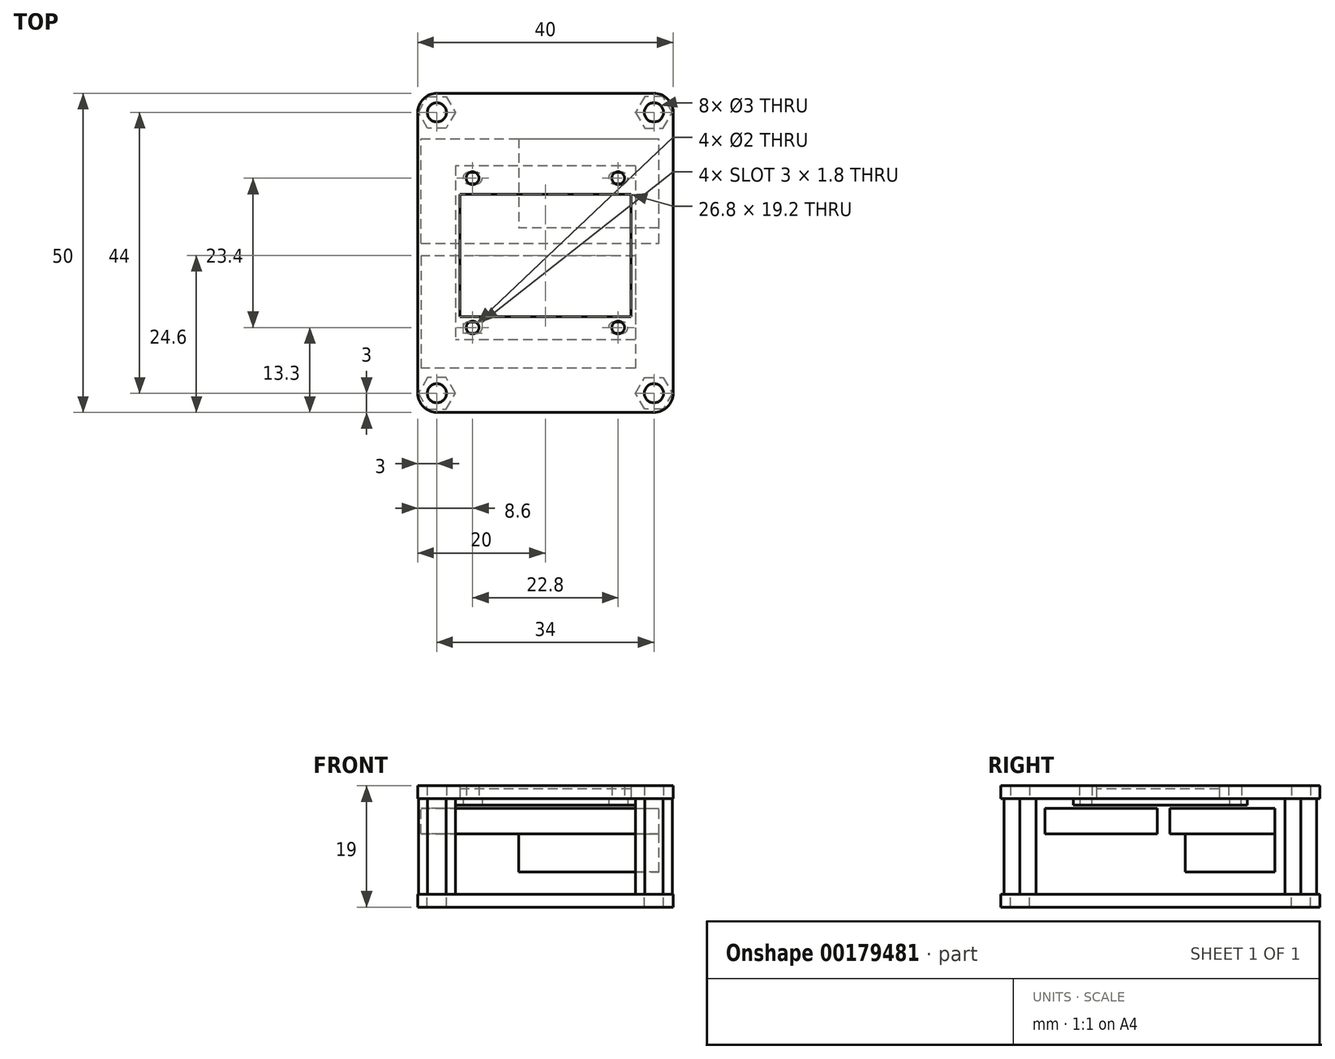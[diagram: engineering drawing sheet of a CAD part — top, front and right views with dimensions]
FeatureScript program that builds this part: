
annotation { "Feature Type Name" : "Feature", "Feature Type Description" : "" }
export const myFeature = defineFeature(function(context is Context, id is Id, definition is map)
    precondition{}
    {
        {
            var Q0;
            Q0=qCreatedBy(makeId("Top.planeOp"),FACE);
            var sketch = newSketch(context, id + "F0", { "sketchPlane" : qUnion([Q0])});
            skLineSegment(sketch, "E0.bottom", {"start": v(14.1, 13.6) * mm, "end": v(-14.1, 13.6) * mm});
            skLineSegment(sketch, "E0.top", {"start": v(14.1, -13.6) * mm, "end": v(-14.1, -13.6) * mm});
            skLineSegment(sketch, "E0.left", {"start": v(14.1, 13.6) * mm, "end": v(14.1, -13.6) * mm});
            skLineSegment(sketch, "E0.right", {"start": v(-14.1, 13.6) * mm, "end": v(-14.1, -13.6) * mm});
            skPoint(sketch, "E0.middle", {"position": v(0, 0) * mm});
            skArc(sketch, "E1", {"start": v(-12, 12.6) * mm, "mid": v(-12.9, 11.7) * mm, "end": v(-12, 10.8) * mm});
            skArc(sketch, "E2", {"start": v(-10.8, 10.8) * mm, "mid": v(-9.9, 11.7) * mm, "end": v(-10.8, 12.6) * mm});
            skPoint(sketch, "E3", {"position": v(-12.9, 11.7) * mm});
            skPoint(sketch, "E4", {"position": v(-9.9, 11.7) * mm});
            skLineSegment(sketch, "E5", {"start": v(-12, 12.6) * mm, "end": v(-10.8, 12.6) * mm});
            skLineSegment(sketch, "E6", {"start": v(-12, 10.8) * mm, "end": v(-10.8, 10.8) * mm});
            skLineSegment(sketch, "E7", {"start": v(0, 0) * mm, "end": v(0, 3.9) * mm, "construction": true});
            skPoint(sketch, "E8.MirrorP", {"position": v(12.9, 11.7) * mm});
            skPoint(sketch, "E9.MirrorP", {"position": v(9.9, 11.7) * mm});
            skLineSegment(sketch, "E10.MirrorCS", {"start": v(12, 10.8) * mm, "end": v(10.8, 10.8) * mm});
            skArc(sketch, "E11.MirrorCS", {"start": v(12, 12.6) * mm, "mid": v(12.9, 11.7) * mm, "end": v(12, 10.8) * mm});
            skArc(sketch, "E12.MirrorCS", {"start": v(10.8, 10.8) * mm, "mid": v(9.9, 11.7) * mm, "end": v(10.8, 12.6) * mm});
            skLineSegment(sketch, "E13.MirrorCS", {"start": v(12, 12.6) * mm, "end": v(10.8, 12.6) * mm});
            skLineSegment(sketch, "E14", {"start": v(0, 0) * mm, "end": v(-3.91, 0) * mm, "construction": true});
            skLineSegment(sketch, "E15.MirrorCS", {"start": v(-12, -12.6) * mm, "end": v(-10.8, -12.6) * mm});
            skLineSegment(sketch, "E16.MirrorCS", {"start": v(-12, -10.8) * mm, "end": v(-10.8, -10.8) * mm});
            skLineSegment(sketch, "E17.MirrorCS", {"start": v(12, -10.8) * mm, "end": v(10.8, -10.8) * mm});
            skLineSegment(sketch, "E18.MirrorCS", {"start": v(12, -12.6) * mm, "end": v(10.8, -12.6) * mm});
            skArc(sketch, "E19.MirrorCS", {"start": v(-12, -12.6) * mm, "mid": v(-12.9, -11.7) * mm, "end": v(-12, -10.8) * mm});
            skArc(sketch, "E20.MirrorCS", {"start": v(-10.8, -10.8) * mm, "mid": v(-9.9, -11.7) * mm, "end": v(-10.8, -12.6) * mm});
            skArc(sketch, "E21.MirrorCS", {"start": v(12, -12.6) * mm, "mid": v(12.9, -11.7) * mm, "end": v(12, -10.8) * mm});
            skArc(sketch, "E22.MirrorCS", {"start": v(10.8, -10.8) * mm, "mid": v(9.9, -11.7) * mm, "end": v(10.8, -12.6) * mm});
            skPoint(sketch, "E23.MirrorP", {"position": v(12.9, -11.7) * mm});
            skPoint(sketch, "E24.MirrorP", {"position": v(-9.9, -11.7) * mm});
            skPoint(sketch, "E25.MirrorP", {"position": v(9.9, -11.7) * mm});
            skPoint(sketch, "E26.MirrorP", {"position": v(-12.9, -11.7) * mm});
            skSolve(sketch);
        }
        {
            var Q0;
            Q0 = qSketchRegion(id + "F0", true);
            extrude(context, id + "F1", {"entities" : qUnion([Q0]), "depth" : 1 * mm});
        }
        {
            var Q0;
            Q0=makeQuery(id+"F1.opExtrude","CAP_FACE",FACE,{"disambiguationData":[OSD([sQuery(id+"F0.wireOp",EDGE,"E0.bottom"),sQuery(id+"F0.wireOp",EDGE,"E0.top"),sQuery(id+"F0.wireOp",EDGE,"E0.left"),sQuery(id+"F0.wireOp",EDGE,"E0.right"),sQuery(id+"F0.wireOp",EDGE,"E1"),sQuery(id+"F0.wireOp",EDGE,"E2"),sQuery(id+"F0.wireOp",EDGE,"E5"),sQuery(id+"F0.wireOp",EDGE,"E6"),sQuery(id+"F0.wireOp",EDGE,"E10.MirrorCS"),sQuery(id+"F0.wireOp",EDGE,"E11.MirrorCS"),sQuery(id+"F0.wireOp",EDGE,"E12.MirrorCS"),sQuery(id+"F0.wireOp",EDGE,"E13.MirrorCS"),sQuery(id+"F0.wireOp",EDGE,"E15.MirrorCS"),sQuery(id+"F0.wireOp",EDGE,"E16.MirrorCS"),sQuery(id+"F0.wireOp",EDGE,"E17.MirrorCS"),sQuery(id+"F0.wireOp",EDGE,"E18.MirrorCS"),sQuery(id+"F0.wireOp",EDGE,"E19.MirrorCS"),sQuery(id+"F0.wireOp",EDGE,"E20.MirrorCS"),sQuery(id+"F0.wireOp",EDGE,"E21.MirrorCS"),sQuery(id+"F0.wireOp",EDGE,"E22.MirrorCS")])],"isStart":false});
            var sketch = newSketch(context, id + "F2", { "sketchPlane" : qUnion([Q0])});
            skLineSegment(sketch, "E27.bottom", {"start": v(13.4, 9.2) * mm, "end": v(-13.4, 9.2) * mm});
            skLineSegment(sketch, "E27.top", {"start": v(13.4, -10) * mm, "end": v(-13.4, -10) * mm});
            skLineSegment(sketch, "E27.left", {"start": v(13.4, 9.2) * mm, "end": v(13.4, -10) * mm});
            skLineSegment(sketch, "E27.right", {"start": v(-13.4, 9.2) * mm, "end": v(-13.4, -10) * mm});
            skPoint(sketch, "E27.middle", {"position": v(0, -0.4) * mm});
            skSolve(sketch);
        }
        {
            var Q0;
            Q0 = qSketchRegion(id + "F2", true);
            extrude(context, id + "F3", {"entities" : qUnion([Q0]), "operationType" : NewBodyOperationType.ADD, "depth" : 1.5 * mm});
        }
        {
            var Q0;
            Q0=makeQuery(id+"F1.opExtrude","CAP_FACE",FACE,{"disambiguationData":[OSD([sQuery(id+"F0.wireOp",EDGE,"E0.bottom"),sQuery(id+"F0.wireOp",EDGE,"E0.top"),sQuery(id+"F0.wireOp",EDGE,"E0.left"),sQuery(id+"F0.wireOp",EDGE,"E0.right"),sQuery(id+"F0.wireOp",EDGE,"E1"),sQuery(id+"F0.wireOp",EDGE,"E2"),sQuery(id+"F0.wireOp",EDGE,"E5"),sQuery(id+"F0.wireOp",EDGE,"E6"),sQuery(id+"F0.wireOp",EDGE,"E10.MirrorCS"),sQuery(id+"F0.wireOp",EDGE,"E11.MirrorCS"),sQuery(id+"F0.wireOp",EDGE,"E12.MirrorCS"),sQuery(id+"F0.wireOp",EDGE,"E13.MirrorCS"),sQuery(id+"F0.wireOp",EDGE,"E15.MirrorCS"),sQuery(id+"F0.wireOp",EDGE,"E16.MirrorCS"),sQuery(id+"F0.wireOp",EDGE,"E17.MirrorCS"),sQuery(id+"F0.wireOp",EDGE,"E18.MirrorCS"),sQuery(id+"F0.wireOp",EDGE,"E19.MirrorCS"),sQuery(id+"F0.wireOp",EDGE,"E20.MirrorCS"),sQuery(id+"F0.wireOp",EDGE,"E21.MirrorCS"),sQuery(id+"F0.wireOp",EDGE,"E22.MirrorCS")])],"isStart":false});
            var sketch = newSketch(context, id + "F4", { "sketchPlane" : qUnion([Q0])});
            skLineSegment(sketch, "E28.bottom", {"start": v(17, 25) * mm, "end": v(-17, 25) * mm});
            skLineSegment(sketch, "E28.top", {"start": v(17, -25) * mm, "end": v(-17, -25) * mm});
            skLineSegment(sketch, "E28.left", {"start": v(20, 22) * mm, "end": v(20, -22) * mm});
            skLineSegment(sketch, "E28.right", {"start": v(-20, 22) * mm, "end": v(-20, -22) * mm});
            skPoint(sketch, "E28.middle", {"position": v(0, 0) * mm});
            skLineSegment(sketch, "E29", {"start": v(-12.9, 11.7) * mm, "end": v(-9.9, 11.7) * mm, "construction": true});
            skCircle(sketch, "E30", {"center": v(-11.4, 11.7) * mm, "radius": 1 * mm});
            skLineSegment(sketch, "E31", {"start": v(0, 0) * mm, "end": v(0, 2.9) * mm, "construction": true});
            skLineSegment(sketch, "E32", {"start": v(0, 0) * mm, "end": v(-3.26, 0) * mm, "construction": true});
            skCircle(sketch, "E33.MirrorC", {"center": v(11.4, 11.7) * mm, "radius": 1 * mm});
            skCircle(sketch, "E34.MirrorC", {"center": v(-11.4, -11.7) * mm, "radius": 1 * mm});
            skCircle(sketch, "E35.MirrorC", {"center": v(11.4, -11.7) * mm, "radius": 1 * mm});
            skCircle(sketch, "E36", {"center": v(-17, 22) * mm, "radius": 1.5 * mm});
            skPoint(sketch, "E37.visualSharp", {"position": v(-20, 25) * mm});
            skArc(sketch, "E37.filletArc", {"start": v(-17, 25) * mm, "mid": v(-19.12, 24.12) * mm, "end": v(-20, 22) * mm});
            skPoint(sketch, "E38.visualSharp", {"position": v(20, 25) * mm});
            skArc(sketch, "E38.filletArc", {"start": v(20, 22) * mm, "mid": v(19.12, 24.12) * mm, "end": v(17, 25) * mm});
            skPoint(sketch, "E39.visualSharp", {"position": v(20, -25) * mm});
            skArc(sketch, "E39.filletArc", {"start": v(17, -25) * mm, "mid": v(19.12, -24.12) * mm, "end": v(20, -22) * mm});
            skPoint(sketch, "E40.visualSharp", {"position": v(-20, -25) * mm});
            skArc(sketch, "E40.filletArc", {"start": v(-20, -22) * mm, "mid": v(-19.12, -24.12) * mm, "end": v(-17, -25) * mm});
            skCircle(sketch, "E41", {"center": v(17, 22) * mm, "radius": 1.5 * mm});
            skCircle(sketch, "E42", {"center": v(-17, -22) * mm, "radius": 1.5 * mm});
            skCircle(sketch, "E43", {"center": v(17, -22) * mm, "radius": 1.5 * mm});
            skLineSegment(sketch, "E44.bottom", {"start": v(-13.4, 9.2) * mm, "end": v(13.4, 9.2) * mm});
            skLineSegment(sketch, "E44.top", {"start": v(-13.4, -10) * mm, "end": v(13.4, -10) * mm});
            skLineSegment(sketch, "E44.left", {"start": v(-13.4, 9.2) * mm, "end": v(-13.4, -10) * mm});
            skLineSegment(sketch, "E44.right", {"start": v(13.4, 9.2) * mm, "end": v(13.4, -10) * mm});
            skSolve(sketch);
        }
        {
            var Q0;
            Q0 = qSketchRegion(id + "F4", true);
            extrude(context, id + "F5", {"entities" : qUnion([Q0]), "depth" : 2 * mm});
        }
        {
            var Q0;
            Q0=makeQuery(id+"F1.opExtrude","CAP_FACE",FACE,{"disambiguationData":[OSD([sQuery(id+"F0.wireOp",EDGE,"E0.bottom"),sQuery(id+"F0.wireOp",EDGE,"E0.top"),sQuery(id+"F0.wireOp",EDGE,"E0.left"),sQuery(id+"F0.wireOp",EDGE,"E0.right"),sQuery(id+"F0.wireOp",EDGE,"E1"),sQuery(id+"F0.wireOp",EDGE,"E2"),sQuery(id+"F0.wireOp",EDGE,"E5"),sQuery(id+"F0.wireOp",EDGE,"E6"),sQuery(id+"F0.wireOp",EDGE,"E10.MirrorCS"),sQuery(id+"F0.wireOp",EDGE,"E11.MirrorCS"),sQuery(id+"F0.wireOp",EDGE,"E12.MirrorCS"),sQuery(id+"F0.wireOp",EDGE,"E13.MirrorCS"),sQuery(id+"F0.wireOp",EDGE,"E15.MirrorCS"),sQuery(id+"F0.wireOp",EDGE,"E16.MirrorCS"),sQuery(id+"F0.wireOp",EDGE,"E17.MirrorCS"),sQuery(id+"F0.wireOp",EDGE,"E18.MirrorCS"),sQuery(id+"F0.wireOp",EDGE,"E19.MirrorCS"),sQuery(id+"F0.wireOp",EDGE,"E20.MirrorCS"),sQuery(id+"F0.wireOp",EDGE,"E21.MirrorCS"),sQuery(id+"F0.wireOp",EDGE,"E22.MirrorCS")])],"isStart":true});
            cPlane(context, id + "F6", {"entities" : qUnion([Q0]), "cplaneType" : CPlaneType.OFFSET, "offset" : 0.5 * mm, "width" : 150 * mm, "height" : 150 * mm});
        }
        {
            var Q0;
            Q0=qCreatedBy(id+"F6.planeOp",FACE);
            var sketch = newSketch(context, id + "F7", { "sketchPlane" : qUnion([Q0])});
            skLineSegment(sketch, "E45.bottom", {"start": v(14.1, 0.5) * mm, "end": v(-19.5, 0.5) * mm});
            skLineSegment(sketch, "E45.top", {"start": v(14.1, 18.1) * mm, "end": v(-19.5, 18.1) * mm});
            skLineSegment(sketch, "E45.left", {"start": v(14.1, 0.5) * mm, "end": v(14.1, 18.1) * mm});
            skLineSegment(sketch, "E45.right", {"start": v(-19.5, 0.5) * mm, "end": v(-19.5, 18.1) * mm});
            skLineSegment(sketch, "E46.0", {"start": v(14.1, -13.6) * mm, "end": v(14.1, 13.6) * mm, "construction": true});
            skLineSegment(sketch, "E47.bottom", {"start": v(-19.5, -1.5) * mm, "end": v(17.8, -1.5) * mm});
            skLineSegment(sketch, "E47.top", {"start": v(-19.5, -17.9) * mm, "end": v(17.8, -17.9) * mm});
            skLineSegment(sketch, "E47.left", {"start": v(-19.5, -1.5) * mm, "end": v(-19.5, -17.9) * mm});
            skLineSegment(sketch, "E47.right", {"start": v(17.8, -1.5) * mm, "end": v(17.8, -17.9) * mm});
            skSolve(sketch);
        }
        {
            var Q0;
            Q0 = qSketchRegion(id + "F7", true);
            extrude(context, id + "F8", {"entities" : qUnion([Q0]), "depth" : 4 * mm});
        }
        {
            var Q0;
            Q0=makeQuery(id+"F8.opExtrude","CAP_FACE",FACE,{"disambiguationData":[OSD([sQuery(id+"F7.wireOp",EDGE,"E47.bottom"),sQuery(id+"F7.wireOp",EDGE,"E47.top"),sQuery(id+"F7.wireOp",EDGE,"E47.left"),sQuery(id+"F7.wireOp",EDGE,"E47.right")])],"isStart":false});
            var sketch = newSketch(context, id + "F9", { "sketchPlane" : qUnion([Q0])});
            skLineSegment(sketch, "E48.bottom", {"start": v(17.8, -17.9) * mm, "end": v(-4.2, -17.9) * mm});
            skLineSegment(sketch, "E48.top", {"start": v(17.8, -3.9) * mm, "end": v(-4.2, -3.9) * mm});
            skLineSegment(sketch, "E48.left", {"start": v(17.8, -17.9) * mm, "end": v(17.8, -3.9) * mm});
            skLineSegment(sketch, "E48.right", {"start": v(-4.2, -17.9) * mm, "end": v(-4.2, -3.9) * mm});
            skSolve(sketch);
        }
        {
            var Q0;
            Q0 = qSketchRegion(id + "F9", true);
            extrude(context, id + "F10", {"entities" : qUnion([Q0]), "depth" : 6 * mm});
        }
        {
            var Q0;
            Q0=makeQuery(id+"F5.opExtrude","CAP_FACE",FACE,{"disambiguationData":[OSD([sQuery(id+"F4.wireOp",EDGE,"E28.bottom"),sQuery(id+"F4.wireOp",EDGE,"E28.top"),sQuery(id+"F4.wireOp",EDGE,"E28.left"),sQuery(id+"F4.wireOp",EDGE,"E28.right"),sQuery(id+"F4.wireOp",EDGE,"E30"),sQuery(id+"F4.wireOp",EDGE,"E33.MirrorC"),sQuery(id+"F4.wireOp",EDGE,"E34.MirrorC"),sQuery(id+"F4.wireOp",EDGE,"E35.MirrorC"),sQuery(id+"F4.wireOp",EDGE,"E36"),sQuery(id+"F4.wireOp",EDGE,"E37.filletArc"),sQuery(id+"F4.wireOp",EDGE,"E38.filletArc"),sQuery(id+"F4.wireOp",EDGE,"E39.filletArc"),sQuery(id+"F4.wireOp",EDGE,"E40.filletArc"),sQuery(id+"F4.wireOp",EDGE,"E41"),sQuery(id+"F4.wireOp",EDGE,"E42"),sQuery(id+"F4.wireOp",EDGE,"E43"),sQuery(id+"F4.wireOp",EDGE,"E44.bottom"),sQuery(id+"F4.wireOp",EDGE,"E44.top"),sQuery(id+"F4.wireOp",EDGE,"E44.left"),sQuery(id+"F4.wireOp",EDGE,"E44.right")])],"isStart":true});
            var sketch = newSketch(context, id + "F11", { "sketchPlane" : qUnion([Q0])});
            skCircle(sketch, "E49.cCircle", {"center": v(-17, 22) * mm, "radius": 2.5 * mm, "construction": true});
            skLineSegment(sketch, "E49.0", {"start": v(-18.44, 24.5) * mm, "end": v(-15.56, 24.5) * mm});
            skLineSegment(sketch, "E49.1", {"start": v(-15.56, 24.5) * mm, "end": v(-14.11, 22) * mm});
            skLineSegment(sketch, "E49.2", {"start": v(-14.11, 22) * mm, "end": v(-15.56, 19.5) * mm});
            skLineSegment(sketch, "E49.3", {"start": v(-15.56, 19.5) * mm, "end": v(-18.44, 19.5) * mm});
            skLineSegment(sketch, "E49.4", {"start": v(-18.44, 19.5) * mm, "end": v(-19.89, 22) * mm});
            skLineSegment(sketch, "E49.5", {"start": v(-19.89, 22) * mm, "end": v(-18.44, 24.5) * mm});
            skPoint(sketch, "E49.0.midPoint", {"position": v(-17, 24.5) * mm});
            skLineSegment(sketch, "E50", {"start": v(0, 0) * mm, "end": v(0, 6.6) * mm, "construction": true});
            skLineSegment(sketch, "E51", {"start": v(0, 0) * mm, "end": v(-7.66, 0) * mm, "construction": true});
            skLineSegment(sketch, "E52.MirrorCS", {"start": v(19.89, 22) * mm, "end": v(18.44, 24.5) * mm});
            skLineSegment(sketch, "E53.MirrorCS", {"start": v(15.56, 19.5) * mm, "end": v(18.44, 19.5) * mm});
            skLineSegment(sketch, "E54.MirrorCS", {"start": v(18.44, 19.5) * mm, "end": v(19.89, 22) * mm});
            skCircle(sketch, "E55.MirrorC", {"center": v(17, 22) * mm, "radius": 2.5 * mm, "construction": true});
            skLineSegment(sketch, "E56.MirrorCS", {"start": v(18.44, 24.5) * mm, "end": v(15.56, 24.5) * mm});
            skLineSegment(sketch, "E57.MirrorCS", {"start": v(15.56, 24.5) * mm, "end": v(14.11, 22) * mm});
            skLineSegment(sketch, "E58.MirrorCS", {"start": v(14.11, 22) * mm, "end": v(15.56, 19.5) * mm});
            skPoint(sketch, "E59.MirrorP", {"position": v(17, 24.5) * mm});
            skPoint(sketch, "E60.MirrorP", {"position": v(-17, -24.5) * mm});
            skCircle(sketch, "E61.MirrorC", {"center": v(-17, -22) * mm, "radius": 2.5 * mm, "construction": true});
            skLineSegment(sketch, "E62.MirrorCS", {"start": v(-18.44, -24.5) * mm, "end": v(-15.56, -24.5) * mm});
            skLineSegment(sketch, "E63.MirrorCS", {"start": v(-15.56, -24.5) * mm, "end": v(-14.11, -22) * mm});
            skLineSegment(sketch, "E64.MirrorCS", {"start": v(-14.11, -22) * mm, "end": v(-15.56, -19.5) * mm});
            skLineSegment(sketch, "E65.MirrorCS", {"start": v(-15.56, -19.5) * mm, "end": v(-18.44, -19.5) * mm});
            skLineSegment(sketch, "E66.MirrorCS", {"start": v(-18.44, -19.5) * mm, "end": v(-19.89, -22) * mm});
            skLineSegment(sketch, "E67.MirrorCS", {"start": v(-19.89, -22) * mm, "end": v(-18.44, -24.5) * mm});
            skLineSegment(sketch, "E68.MirrorCS", {"start": v(14.11, -22) * mm, "end": v(15.56, -19.5) * mm});
            skLineSegment(sketch, "E69.MirrorCS", {"start": v(15.56, -24.5) * mm, "end": v(14.11, -22) * mm});
            skLineSegment(sketch, "E70.MirrorCS", {"start": v(15.56, -19.5) * mm, "end": v(18.44, -19.5) * mm});
            skLineSegment(sketch, "E71.MirrorCS", {"start": v(18.44, -19.5) * mm, "end": v(19.89, -22) * mm});
            skLineSegment(sketch, "E72.MirrorCS", {"start": v(18.44, -24.5) * mm, "end": v(15.56, -24.5) * mm});
            skLineSegment(sketch, "E73.MirrorCS", {"start": v(19.89, -22) * mm, "end": v(18.44, -24.5) * mm});
            skPoint(sketch, "E74.MirrorP", {"position": v(17, -24.5) * mm});
            skCircle(sketch, "E75.MirrorC", {"center": v(17, -22) * mm, "radius": 2.5 * mm, "construction": true});
            skSolve(sketch);
        }
        {
            var Q0;
            Q0 = qSketchRegion(id + "F11", true);
            extrude(context, id + "F12", {"entities" : qUnion([Q0]), "depth" : 15 * mm});
        }
        {
            var Q0;
            Q0=makeQuery(id+"F12.opExtrude","CAP_FACE",FACE,{"disambiguationData":[OSD([sQuery(id+"F11.wireOp",EDGE,"E49.0"),sQuery(id+"F11.wireOp",EDGE,"E49.1"),sQuery(id+"F11.wireOp",EDGE,"E49.2"),sQuery(id+"F11.wireOp",EDGE,"E49.3"),sQuery(id+"F11.wireOp",EDGE,"E49.4"),sQuery(id+"F11.wireOp",EDGE,"E49.5")])],"isStart":false});
            var sketch = newSketch(context, id + "F13", { "sketchPlane" : qUnion([Q0])});
            skLineSegment(sketch, "E76.0", {"start": v(17, 25) * mm, "end": v(-17, 25) * mm});
            skArc(sketch, "E76.1", {"start": v(-20, 22) * mm, "mid": v(-19.12, 24.12) * mm, "end": v(-17, 25) * mm});
            skLineSegment(sketch, "E76.2", {"start": v(-20, -22) * mm, "end": v(-20, 22) * mm});
            skArc(sketch, "E76.3", {"start": v(-17, -25) * mm, "mid": v(-19.12, -24.12) * mm, "end": v(-20, -22) * mm});
            skLineSegment(sketch, "E76.4", {"start": v(17, -25) * mm, "end": v(-17, -25) * mm});
            skArc(sketch, "E76.5", {"start": v(20, -22) * mm, "mid": v(19.12, -24.12) * mm, "end": v(17, -25) * mm});
            skLineSegment(sketch, "E76.6", {"start": v(20, -22) * mm, "end": v(20, 22) * mm});
            skArc(sketch, "E76.7", {"start": v(17, 25) * mm, "mid": v(19.12, 24.12) * mm, "end": v(20, 22) * mm});
            skCircle(sketch, "E77.0", {"center": v(17, 22) * mm, "radius": 1.5 * mm});
            skCircle(sketch, "E77.1", {"center": v(-17, 22) * mm, "radius": 1.5 * mm});
            skCircle(sketch, "E77.2", {"center": v(17, -22) * mm, "radius": 1.5 * mm});
            skCircle(sketch, "E77.3", {"center": v(-17, -22) * mm, "radius": 1.5 * mm});
            skSolve(sketch);
        }
        {
            var Q0;
            Q0 = qSketchRegion(id + "F13", true);
            extrude(context, id + "F14", {"entities" : qUnion([Q0]), "depth" : 2 * mm});
        }
    });
